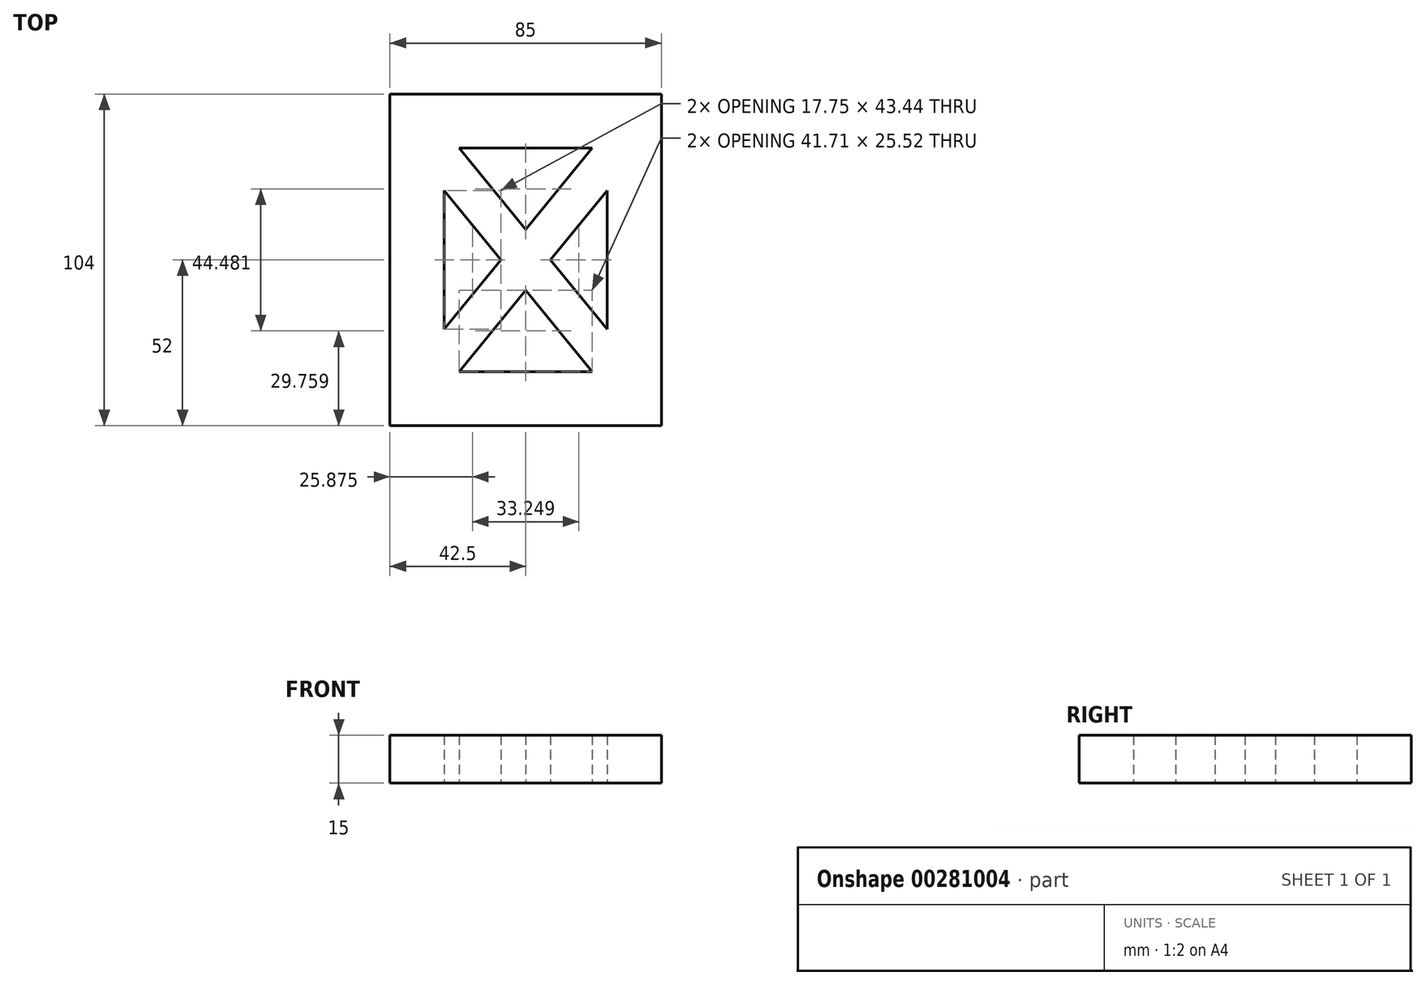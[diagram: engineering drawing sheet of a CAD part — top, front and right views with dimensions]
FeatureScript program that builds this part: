
annotation { "Feature Type Name" : "Feature", "Feature Type Description" : "" }
export const myFeature = defineFeature(function(context is Context, id is Id, definition is map)
    precondition{}
    {
        {
            var Q0;
            Q0=qCreatedBy(makeId("Top.planeOp"),FACE);
            var sketch = newSketch(context, id + "F0", { "sketchPlane" : qUnion([Q0])});
            skLineSegment(sketch, "E0.bottom", {"start": v(42.5, -52) * mm, "end": v(-42.5, -52) * mm});
            skLineSegment(sketch, "E0.top", {"start": v(42.5, 52) * mm, "end": v(-42.5, 52) * mm});
            skLineSegment(sketch, "E0.left", {"start": v(42.5, -52) * mm, "end": v(42.5, 52) * mm});
            skLineSegment(sketch, "E0.right", {"start": v(-42.5, -52) * mm, "end": v(-42.5, 52) * mm});
            skPoint(sketch, "E0.middle", {"position": v(0, 0) * mm});
            skLineSegment(sketch, "E1.bottom", {"start": v(20.86, -35) * mm, "end": v(-20.86, -35) * mm});
            skLineSegment(sketch, "E1.top", {"start": v(20.86, 35) * mm, "end": v(-20.86, 35) * mm});
            skLineSegment(sketch, "E2", {"start": v(3.87, 4.74) * mm, "end": v(-3.87, -4.74) * mm});
            skLineSegment(sketch, "E3", {"start": v(-3.87, 4.74) * mm, "end": v(3.87, -4.74) * mm});
            skLineSegment(sketch, "E4", {"start": v(-25.5, 21.72) * mm, "end": v(20.86, -35) * mm});
            skLineSegment(sketch, "E5", {"start": v(-20.86, 35) * mm, "end": v(25.5, -21.72) * mm});
            skLineSegment(sketch, "E6", {"start": v(-25.5, -21.72) * mm, "end": v(20.86, 35) * mm});
            skLineSegment(sketch, "E7", {"start": v(-20.86, -35) * mm, "end": v(25.5, 21.72) * mm});
            skPoint(sketch, "E8.orphan", {"position": v(-25.5, 35) * mm});
            skPoint(sketch, "E9.trimOffspring.end.orphan", {"position": v(25.5, 35) * mm});
            skLineSegment(sketch, "E10.trimOffspring", {"start": v(25.5, -21.72) * mm, "end": v(25.5, 21.72) * mm});
            skLineSegment(sketch, "E11.trimOffspring", {"start": v(-25.5, -21.72) * mm, "end": v(-25.5, 21.72) * mm});
            skPoint(sketch, "E1.right.start.orphan", {"position": v(-25.5, -35) * mm});
            skPoint(sketch, "E1.left.start.orphan", {"position": v(25.5, -35) * mm});
            skSolve(sketch);
        }
        {
            var Q0;
            Q0=makeQuery(id+"F0.imprint","IMPRINT",FACE,{"disambiguationData":[TD([[makeQuery(id+"F0.imprint","IMPRINT",EDGE,{"derivedFrom":sQuery(id+"F0.wireOp",EDGE,"E0.bottom")}),-1.0]])]});
            var Q1;
            {var subQ0=sQuery(id+"F0.wireOp",EDGE,"E4");var subQ1=sQuery(id+"F0.wireOp",EDGE,"E2");var subQ2=makeQuery(id+"F0.imprint","INTERSECT",VERTEX,{"derivedFrom":[subQ1,subQ0]});Q1=makeQuery(id+"F0.imprint","IMPRINT",FACE,{"disambiguationData":[TD([[makeQuery(id+"F0.imprint","IMPRINT",EDGE,{"disambiguationData":[TD([[subQ2,1.0]])],"derivedFrom":subQ1}),1.0]])]});}
            var Q2;
            {var subQ0=sQuery(id+"F0.wireOp",EDGE,"E5");var subQ1=sQuery(id+"F0.wireOp",EDGE,"E2");var subQ2=makeQuery(id+"F0.imprint","INTERSECT",VERTEX,{"derivedFrom":[subQ1,subQ0]});Q2=makeQuery(id+"F0.imprint","IMPRINT",FACE,{"disambiguationData":[TD([[makeQuery(id+"F0.imprint","IMPRINT",EDGE,{"disambiguationData":[TD([[subQ2,-1.0]])],"derivedFrom":subQ1}),-1.0]])]});}
            var Q3;
            {var subQ0=sQuery(id+"F0.wireOp",EDGE,"E5");var subQ1=sQuery(id+"F0.wireOp",EDGE,"E2");var subQ2=makeQuery(id+"F0.imprint","INTERSECT",VERTEX,{"derivedFrom":[subQ1,subQ0]});Q3=makeQuery(id+"F0.imprint","IMPRINT",FACE,{"disambiguationData":[TD([[makeQuery(id+"F0.imprint","IMPRINT",EDGE,{"disambiguationData":[TD([[subQ2,-1.0]])],"derivedFrom":subQ1}),1.0]])]});}
            var Q4;
            {var subQ0=sQuery(id+"F0.wireOp",EDGE,"E4");var subQ1=sQuery(id+"F0.wireOp",EDGE,"E2");var subQ2=makeQuery(id+"F0.imprint","INTERSECT",VERTEX,{"derivedFrom":[subQ1,subQ0]});Q4=makeQuery(id+"F0.imprint","IMPRINT",FACE,{"disambiguationData":[TD([[makeQuery(id+"F0.imprint","IMPRINT",EDGE,{"disambiguationData":[TD([[subQ2,1.0]])],"derivedFrom":subQ1}),-1.0]])]});}
            extrude(context, id + "F1", {"entities" : qUnion([Q0, Q1, Q2, Q3, Q4]), "depth" : 15 * mm});
        }
    });
